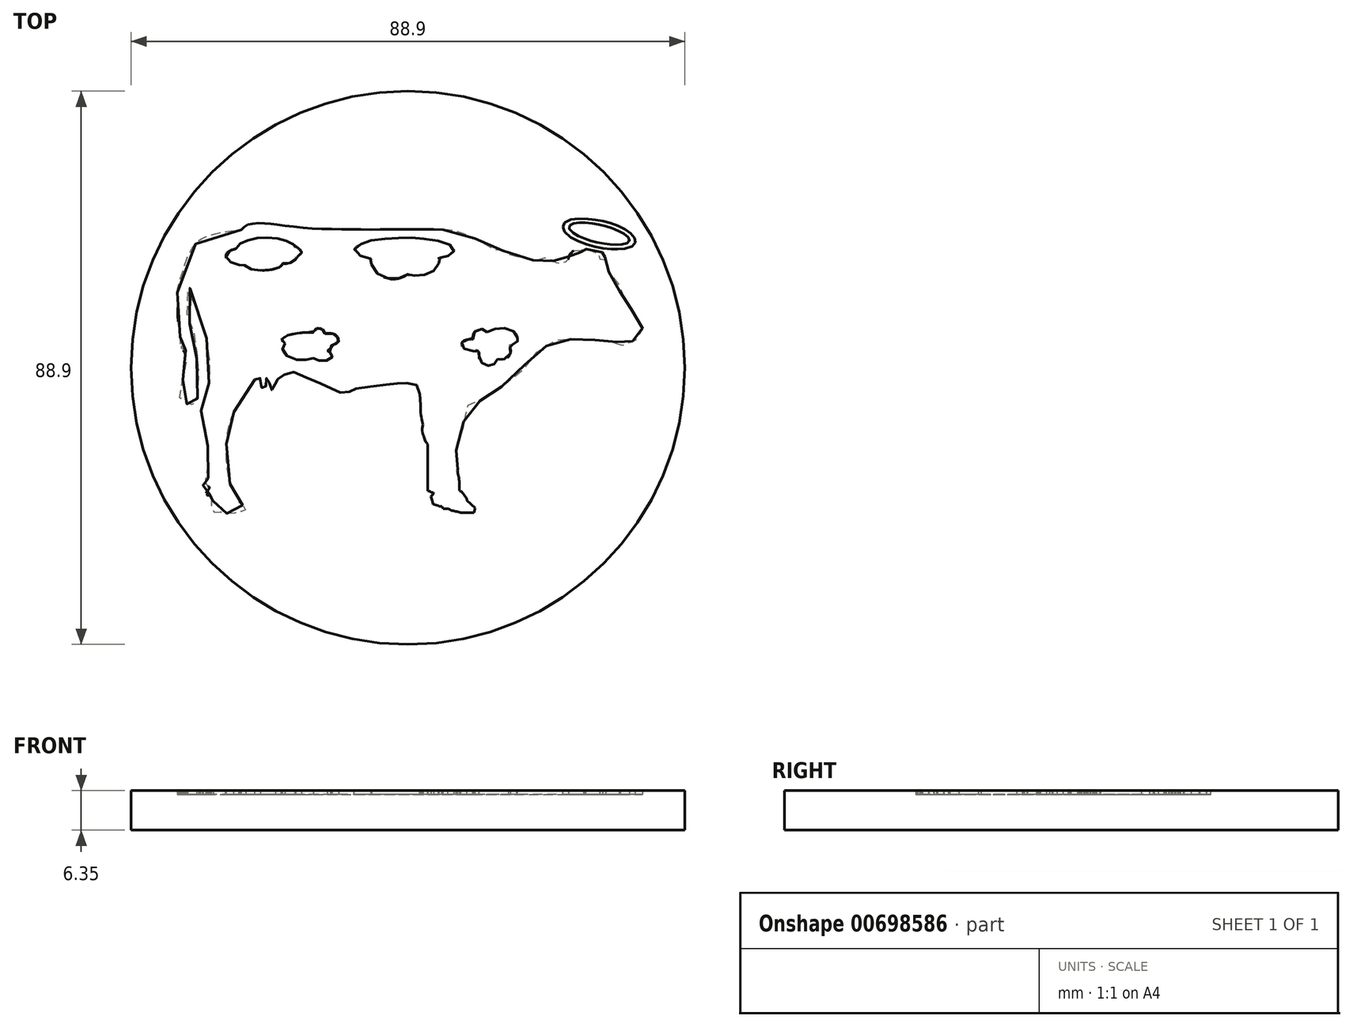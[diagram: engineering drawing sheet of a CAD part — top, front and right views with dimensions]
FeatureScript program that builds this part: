
annotation { "Feature Type Name" : "Feature", "Feature Type Description" : "" }
export const myFeature = defineFeature(function(context is Context, id is Id, definition is map)
    precondition{}
    {
        {
            var Q0;
            Q0=qCreatedBy(makeId("Top.planeOp"),FACE);
            var sketch = newSketch(context, id + "F0", { "sketchPlane" : qUnion([Q0])});
            skCircle(sketch, "E0", {"center": v(0, 0) * mm, "radius": 44.45 * mm});
            skSolve(sketch);
        }
        {
            var Q0;
            Q0=makeQuery(id+"F0.imprint","IMPRINT",FACE,{"disambiguationData":[TD([[makeQuery(id+"F0.imprint","IMPRINT",EDGE,{"derivedFrom":sQuery(id+"F0.wireOp",EDGE,"E0")}),1.0]])]});
            extrude(context, id + "F1", {"entities" : qUnion([Q0]), "depth" : 6.35 * mm, "offsetDistance" : 25.4 * mm});
        }
        {
            var Q0;
            Q0=makeQuery(id+"F1.opExtrude","CAP_FACE",FACE,{"disambiguationData":[OSD([sQuery(id+"F0.wireOp",EDGE,"E0")])],"isStart":false});
            var sketch = newSketch(context, id + "F2", { "sketchPlane" : qUnion([Q0])});
            skFitSpline(sketch, "E1", {"points": [v(-26.75, 22.15) * mm, v(-26.37, 22.53) * mm, v(-25.86, 22.91) * mm, v(-25.23, 23.1) * mm, v(-24.18, 23.23) * mm, v(-22.81, 23.17) * mm, v(-21.67, 23.07) * mm, v(-19.9, 22.85) * mm, v(-17.06, 22.53) * mm, v(-14.24, 22.34) * mm, v(-10.9, 22.28) * mm, v(-7.82, 22.22) * mm, v(-4.65, 22.22) * mm, v(-0.3, 22.25) * mm, v(5.62, 22.16) * mm], "startDerivative": vector(10.6, 11) * mm, "endDerivative": vector(16.74, -2.24) * mm});
            skFitSpline(sketch, "E2", {"points": [v(5.62, 22.16) * mm, v(7.08, 22.16) * mm, v(8.96, 21.52) * mm, v(10.79, 20.75) * mm, v(12.81, 19.7) * mm, v(13.87, 19.07) * mm, v(15.07, 18.87) * mm, v(15.6, 18.58) * mm, v(16.71, 18.1) * mm, v(18.5, 17.72) * mm, v(20.8, 17.19) * mm, v(21.24, 17.43) * mm, v(21.82, 17.67) * mm, v(22.63, 17.57) * mm, v(23.16, 17.28) * mm, v(23.64, 16.95) * mm, v(24.51, 16.85) * mm, v(25.28, 17.04) * mm, v(25.72, 17.33) * mm, v(25.76, 17.72) * mm, v(26.05, 18.3) * mm, v(26.53, 18.78) * mm, v(26.82, 18.97) * mm, v(27.4, 18.54) * mm, v(27.64, 18.15) * mm, v(27.74, 18.92) * mm, v(27.98, 18.68) * mm, v(28.27, 18.87) * mm, v(28.22, 19.02) * mm, v(28.32, 19.3) * mm, v(28.5, 19.55) * mm, v(28.5, 19.11) * mm, v(28.9, 19.11) * mm, v(29.57, 18.92) * mm, v(30.34, 18.54) * mm, v(30.58, 18.34) * mm, v(30.87, 18.54) * mm, v(31.1, 18.63) * mm, v(31.2, 18.34) * mm, v(30.92, 17.81) * mm, v(30.82, 17.48) * mm, v(30.92, 17.28) * mm, v(31.06, 17.57) * mm, v(31.3, 17.72) * mm, v(31.59, 17.81) * mm, v(31.73, 17.62) * mm, v(31.69, 17.33) * mm, v(31.25, 17.04) * mm, v(31.54, 16.75) * mm, v(31.83, 16.13) * mm, v(32.36, 15.31) * mm, v(32.8, 14.97) * mm, v(33.8, 13.82) * mm, v(33.9, 13.43) * mm, v(33.9, 12.7) * mm, v(34.1, 11.84) * mm, v(34.1, 11.55) * mm, v(34.72, 10.98) * mm, v(35.15, 10.4) * mm, v(35.78, 9.58) * mm, v(36.36, 8.76) * mm, v(37.22, 7.85) * mm, v(37.66, 7.17) * mm, v(37.66, 6.88) * mm, v(37.6, 5.78) * mm, v(37.18, 5.3) * mm, v(37.03, 5.3) * mm, v(36.84, 4.67) * mm, v(36.45, 4.43) * mm, v(36.07, 4.33) * mm, v(36.02, 4.1) * mm, v(35.4, 3.66) * mm, v(34.48, 3.56) * mm, v(34.1, 3.66) * mm, v(33.7, 3.85) * mm, v(33.42, 4.24) * mm, v(32.99, 4.14) * mm, v(32.12, 4.24) * mm, v(30.96, 4.38) * mm, v(30.34, 4.43) * mm, v(29.13, 4.62) * mm, v(28.22, 5) * mm, v(27.64, 4.76) * mm, v(26.49, 4.62) * mm, v(25.38, 4.62) * mm, v(24.7, 4.72) * mm, v(23.6, 4.28) * mm, v(22.3, 3.56) * mm, v(21.14, 2.84) * mm, v(19.8, 1.78) * mm, v(19.07, 1.1) * mm, v(18.35, -0.48) * mm, v(17.34, -1.6) * mm, v(15.94, -2.5) * mm, v(14.4, -3.42) * mm, v(13.87, -3.8) * mm, v(12.76, -4.62) * mm, v(12, -5.15) * mm, v(10.6, -5.64) * mm, v(9.58, -6.07) * mm, v(9.15, -7.51) * mm, v(8.86, -9.1) * mm, v(8.62, -10.74) * mm, v(8.28, -11.9) * mm, v(7.75, -13.24) * mm], "startDerivative": vector(72.15, 3.33) * mm, "endDerivative": vector(-42.6, -105.18) * mm});
            skLineSegment(sketch, "E3", {"start": v(7.75, -13.24) * mm, "end": v(7.97, -16.36) * mm});
            skFitSpline(sketch, "E4", {"points": [v(7.97, -16.36) * mm, v(7.97, -16.72) * mm, v(8.11, -17.41) * mm, v(8.24, -18.18) * mm, v(8.28, -18.83) * mm, v(8.32, -19.72) * mm, v(8.52, -19.88) * mm, v(8.96, -20.35) * mm, v(9.37, -20.98) * mm, v(9.47, -21.3) * mm], "startDerivative": vector(-0.27, -3.83) * mm, "endDerivative": vector(0.8, -3.53) * mm});
            skLineSegment(sketch, "E5", {"start": v(9.47, -21.3) * mm, "end": v(10.79, -22.54) * mm});
            skLineSegment(sketch, "E6", {"start": v(10.79, -22.54) * mm, "end": v(10.6, -23.28) * mm});
            skFitSpline(sketch, "E7", {"points": [v(10.6, -23.28) * mm, v(10, -23.28) * mm, v(9.13, -23.28) * mm, v(8.64, -23.28) * mm, v(7.87, -23.12) * mm, v(7.02, -22.92) * mm, v(6.43, -22.66) * mm], "startDerivative": vector(-3.63, -0.02) * mm, "endDerivative": vector(-3.47, 1.8) * mm});
            skLineSegment(sketch, "E8", {"start": v(6.43, -22.66) * mm, "end": v(5.62, -22.66) * mm});
            skLineSegment(sketch, "E9", {"start": v(5.62, -22.66) * mm, "end": v(5.44, -22.27) * mm});
            skFitSpline(sketch, "E10", {"points": [v(5.44, -22.27) * mm, v(5.06, -22.27) * mm, v(4.61, -22.07) * mm, v(4.27, -21.97) * mm, v(4.09, -21.93) * mm, v(3.92, -21.48) * mm, v(3.82, -21.08) * mm, v(3.7, -20.71) * mm, v(3.86, -20.47) * mm, v(4.1, -20.15) * mm, v(4.03, -20.07) * mm, v(3.78, -20.07) * mm, v(3.64, -19.92) * mm, v(3.44, -19.82) * mm, v(3.17, -19.8) * mm], "startDerivative": vector(-4.76, -0.6) * mm, "endDerivative": vector(-4.06, 0.05) * mm});
            skLineSegment(sketch, "E11", {"start": v(3.17, -19.8) * mm, "end": v(3.17, -12.8) * mm});
            skFitSpline(sketch, "E12", {"points": [v(3.17, -12.8) * mm, v(3.17, -12.33) * mm, v(2.91, -11.97) * mm, v(2.59, -11.16) * mm, v(2.39, -10.63) * mm, v(2.28, -9.8) * mm, v(2.4, -9.05) * mm, v(2.26, -8.55) * mm, v(2.1, -7.58) * mm, v(2.02, -6.79) * mm, v(2.02, -5.92) * mm], "startDerivative": vector(0.9, 6.21) * mm, "endDerivative": vector(0.15, 7.98) * mm});
            skFitSpline(sketch, "E13", {"points": [v(2.02, -5.92) * mm, v(2.02, -5.28) * mm, v(2.02, -4.67) * mm, v(1.82, -3.82) * mm, v(1.8, -2.9) * mm, v(1.45, -2.8) * mm, v(0.93, -2.6) * mm, v(0.69, -2.44) * mm, v(-0.35, -2.44) * mm, v(-0.87, -2.42) * mm, v(-1.46, -2.46) * mm, v(-1.9, -2.5) * mm, v(-2.61, -2.54) * mm, v(-3.32, -2.67) * mm, v(-4.74, -2.85) * mm, v(-6.32, -3.1) * mm, v(-7.43, -3.21) * mm, v(-8.53, -3.4) * mm, v(-8.9, -3.4) * mm, v(-9.13, -3.58) * mm, v(-9.36, -3.82) * mm, v(-9.88, -3.84) * mm, v(-10.25, -3.8) * mm, v(-10.8, -3.96) * mm, v(-11.36, -4) * mm, v(-11.9, -3.62) * mm, v(-12.37, -3.3) * mm, v(-12.98, -2.99) * mm, v(-14.03, -2.5) * mm, v(-15.1, -2.06) * mm, v(-16.74, -1.38) * mm, v(-17.84, -0.78) * mm, v(-18.56, -0.7) * mm, v(-19.14, -0.85) * mm, v(-19.61, -1.02) * mm, v(-20.2, -1.2) * mm, v(-20.36, -1.42) * mm, v(-20.57, -1.65) * mm, v(-20.89, -1.83) * mm, v(-21.12, -2) * mm, v(-21.27, -2.05) * mm, v(-21.3, -2.33) * mm, v(-21.32, -2.69) * mm, v(-21.37, -3.12) * mm, v(-21.45, -3.37) * mm, v(-21.63, -3.53) * mm, v(-21.95, -3.53) * mm, v(-22.15, -3.27) * mm, v(-22.25, -2.8) * mm, v(-22.33, -2.17) * mm, v(-22.43, -1.53) * mm, v(-22.56, -1.52) * mm, v(-22.67, -1.52) * mm, v(-22.7, -1.64) * mm, v(-22.72, -1.94) * mm, v(-22.73, -2.46) * mm, v(-22.78, -2.82) * mm, v(-22.84, -3.15) * mm, v(-22.97, -3.44) * mm, v(-23.28, -3.47) * mm, v(-23.44, -3.28) * mm, v(-23.63, -2.76) * mm, v(-23.72, -2.17) * mm, v(-23.74, -1.7) * mm, v(-23.96, -1.55) * mm, v(-24.14, -1.45) * mm, v(-24.3, -1.45) * mm, v(-24.6, -1.87) * mm], "startDerivative": vector(-0.98, 38.8) * mm, "endDerivative": vector(-19.04, -36.66) * mm});
            skLineSegment(sketch, "E14", {"start": v(-24.6, -1.87) * mm, "end": v(-27.93, -7.08) * mm});
            skFitSpline(sketch, "E15", {"points": [v(-27.93, -7.08) * mm, v(-28.21, -7.77) * mm, v(-28.5, -8.4) * mm, v(-28.68, -9) * mm, v(-28.92, -9.97) * mm, v(-29.04, -10.97) * mm, v(-29.17, -12.14) * mm, v(-29.23, -13.31) * mm, v(-29.2, -14.8) * mm, v(-29.09, -16.15) * mm, v(-28.86, -17.38) * mm, v(-28.58, -18.58) * mm, v(-28.28, -19.49) * mm, v(-27.79, -20.06) * mm, v(-27.42, -20.52) * mm, v(-27.14, -20.93) * mm, v(-27.12, -21.43) * mm, v(-27.18, -21.58) * mm, v(-26.9, -21.72) * mm, v(-26.57, -22.02) * mm, v(-26.29, -22.33) * mm, v(-26.07, -22.59) * mm, v(-26.19, -22.93) * mm, v(-26.39, -23.07) * mm, v(-26.71, -23.07) * mm, v(-27.12, -23.18) * mm, v(-27.93, -23.34) * mm, v(-28.74, -23.38) * mm, v(-29.75, -23.34) * mm, v(-30.22, -23.2) * mm, v(-30.74, -23.22) * mm, v(-31.05, -23.28) * mm, v(-31.3, -22.77) * mm, v(-31.55, -22.22) * mm, v(-31.55, -21.7) * mm, v(-31.41, -21.41) * mm, v(-31.27, -21.33) * mm, v(-31.29, -21.25) * mm, v(-31.43, -21.25) * mm, v(-31.7, -21.15) * mm, v(-31.63, -20.97) * mm, v(-31.6, -20.85) * mm, v(-31.61, -20.67) * mm, v(-31.73, -20.54) * mm, v(-31.82, -20.42) * mm, v(-32.02, -20.48) * mm, v(-32.24, -20.48) * mm, v(-32.3, -20.46) * mm, v(-32.18, -20.34) * mm, v(-32.02, -20.26) * mm, v(-31.88, -20.1) * mm, v(-32, -20.06) * mm, v(-32.18, -20.06) * mm, v(-32.34, -20.06) * mm, v(-32.44, -20.08) * mm, v(-32.36, -19.96) * mm, v(-32.16, -19.77) * mm, v(-32, -19.53) * mm, v(-31.88, -19.19) * mm, v(-32.12, -19.07) * mm, v(-32.48, -18.96) * mm, v(-32.83, -18.88) * mm, v(-33, -18.88) * mm, v(-32.75, -18.7) * mm, v(-32.56, -18.62) * mm, v(-32.38, -18.5) * mm, v(-32.28, -18.42) * mm, v(-32.73, -18.36) * mm, v(-32.87, -18.32) * mm, v(-32.9, -18.18) * mm, v(-32.69, -18.16) * mm, v(-32.5, -18.01) * mm, v(-32.38, -17.9) * mm, v(-32.16, -17.87) * mm, v(-32.1, -17.3) * mm, v(-32.1, -16.54) * mm, v(-32.08, -15.8) * mm, v(-32.08, -14.9) * mm, v(-32.12, -14) * mm, v(-32.12, -13.17) * mm, v(-32.18, -12.24) * mm, v(-32.26, -11.53) * mm, v(-32.36, -10.54) * mm, v(-32.5, -9.4) * mm, v(-32.85, -8.1) * mm, v(-33.2, -7.08) * mm, v(-33.35, -6.17) * mm, v(-33.32, -5.76) * mm, v(-33.04, -5.21) * mm, v(-32.51, -4.75) * mm, v(-32.45, -4.49) * mm, v(-32.23, -3.6) * mm, v(-31.94, -2.54) * mm, v(-31.7, -1.49) * mm, v(-31.66, -0.48) * mm, v(-31.74, 0.47) * mm, v(-32.06, 3) * mm, v(-32.47, 5.21) * mm, v(-32.9, 7.02) * mm, v(-33.1, 7.53) * mm, v(-34.17, 10.74) * mm, v(-35.08, 12.83) * mm, v(-35.28, 12.48) * mm, v(-35.43, 11.57) * mm, v(-35.54, 10.42) * mm, v(-35.54, 8.8) * mm, v(-35.31, 7.7) * mm, v(-34.74, 6.44) * mm, v(-34.37, 5.67) * mm, v(-34.1, 4.7) * mm, v(-33.97, 3.58) * mm, v(-33.94, 2.46) * mm, v(-33.9, 1.35) * mm, v(-33.76, 0.4) * mm, v(-33.65, -0.63) * mm, v(-33.6, -2.29) * mm, v(-33.68, -3.66) * mm, v(-33.82, -4.98) * mm, v(-33.97, -5.3) * mm, v(-34.17, -5.53) * mm, v(-34.42, -5.55) * mm, v(-34.6, -5.87) * mm, v(-34.77, -6.16) * mm, v(-35.11, -6.3) * mm, v(-35.25, -6.07) * mm, v(-35.37, -5.67) * mm, v(-35.37, -5.47) * mm, v(-35.6, -5.9) * mm, v(-35.97, -5.98) * mm, v(-36.34, -5.78) * mm, v(-36.54, -5.44) * mm, v(-36.66, -4.75) * mm, v(-36.66, -3.95) * mm, v(-36.37, -2.86) * mm, v(-36.08, -1.63) * mm, v(-35.91, -0.57) * mm, v(-35.68, 0.69) * mm, v(-35.51, 1.35) * mm, v(-35.68, 1.35) * mm, v(-35.74, 1.6) * mm, v(-35.74, 1.98) * mm, v(-35.71, 2.84) * mm, v(-36.03, 2.63) * mm, v(-36.06, 2.92) * mm, v(-36.03, 3.24) * mm, v(-36.28, 3.04) * mm, v(-36.28, 3.52) * mm, v(-36.26, 3.9) * mm, v(-36.46, 3.64) * mm, v(-36.51, 4.3) * mm, v(-36.63, 5.53) * mm, v(-36.77, 6.61) * mm, v(-36.94, 8.19) * mm, v(-36.97, 10.22) * mm, v(-37.03, 12) * mm, v(-36.74, 13.57) * mm, v(-36.14, 15.52) * mm, v(-35.29, 18) * mm, v(-34.03, 19.98) * mm, v(-32.97, 20.84) * mm, v(-30.97, 21.52) * mm, v(-28.89, 21.9) * mm, v(-26.75, 22.15) * mm], "startDerivative": vector(-40.9, -104.55) * mm, "endDerivative": vector(191.28, 19.96) * mm});
            skFitSpline(sketch, "E16", {"points": [v(-27.53, 19.17) * mm, v(-27.4, 19.48) * mm, v(-26.95, 19.94) * mm, v(-26.25, 20.3) * mm, v(-25.46, 20.56) * mm, v(-24.18, 20.85) * mm, v(-23.08, 20.9) * mm, v(-21.73, 20.85) * mm, v(-20.4, 20.66) * mm, v(-19.54, 20.42) * mm, v(-18.7, 20.06) * mm, v(-18.28, 19.67) * mm, v(-18.1, 19.38) * mm, v(-17.47, 19.19) * mm, v(-17.2, 18.95) * mm, v(-17.03, 18.56) * mm, v(-17.08, 18.27) * mm, v(-17.51, 17.96) * mm, v(-18.1, 17.77) * mm, v(-17.97, 17.6) * mm, v(-18.1, 17.31) * mm, v(-18.48, 17.05) * mm, v(-19.22, 16.78) * mm, v(-19.9, 16.73) * mm, v(-20.1, 16.78) * mm, v(-20.28, 16.5) * mm, v(-20.7, 16.16) * mm, v(-21.41, 15.87) * mm, v(-22.62, 15.7) * mm, v(-23.92, 15.65) * mm, v(-25.07, 15.84) * mm, v(-25.97, 16.2) * mm, v(-26.25, 16.52) * mm, v(-26.45, 16.5) * mm, v(-27, 16.52) * mm, v(-27.93, 16.76) * mm, v(-28.66, 17.17) * mm, v(-29.17, 17.7) * mm, v(-29.22, 18.18) * mm, v(-28.83, 18.64) * mm, v(-28.18, 18.97) * mm, v(-27.53, 19.17) * mm]});
            skFitSpline(sketch, "E17", {"points": [v(-19.28, 5.22) * mm, v(-18.55, 5.42) * mm, v(-17.65, 5.58) * mm, v(-16.88, 5.65) * mm, v(-15.96, 5.68) * mm, v(-15.1, 5.68) * mm, v(-15.1, 5.83) * mm, v(-15.06, 5.99) * mm, v(-14.94, 6.12) * mm, v(-14.74, 6.26) * mm, v(-14.5, 6.33) * mm, v(-14.22, 6.36) * mm, v(-13.97, 6.3) * mm, v(-13.78, 6.2) * mm, v(-13.61, 5.99) * mm, v(-13.5, 5.75) * mm, v(-13.42, 5.53) * mm, v(-13.1, 5.5) * mm, v(-12.49, 5.54) * mm, v(-11.9, 5.46) * mm, v(-11.52, 5.24) * mm, v(-11.31, 4.96) * mm, v(-11.28, 4.78) * mm, v(-11.14, 4.62) * mm, v(-11.07, 4.45) * mm, v(-11.13, 4.22) * mm, v(-11.38, 3.96) * mm, v(-11.65, 3.82) * mm, v(-11.96, 3.69) * mm, v(-12.35, 3.6) * mm, v(-12.32, 3.48) * mm, v(-12.33, 3.3) * mm, v(-12.5, 3.06) * mm, v(-12.91, 2.67) * mm, v(-12.7, 2.6) * mm, v(-12.35, 2.4) * mm, v(-12.18, 2.14) * mm, v(-12.13, 1.85) * mm, v(-12.23, 1.6) * mm, v(-12.68, 1.27) * mm, v(-13.13, 1.13) * mm, v(-13.8, 1.13) * mm, v(-14.17, 1.13) * mm, v(-14.67, 1.3) * mm, v(-14.94, 1.58) * mm, v(-15.2, 1.53) * mm, v(-15.72, 1.34) * mm, v(-16.18, 1.29) * mm, v(-16.88, 1.29) * mm, v(-17.65, 1.29) * mm, v(-18.6, 1.5) * mm, v(-19.55, 1.99) * mm, v(-20.05, 2.51) * mm, v(-20.15, 2.99) * mm, v(-19.98, 3.45) * mm, v(-19.69, 3.8) * mm, v(-19.84, 3.9) * mm, v(-20.18, 4.1) * mm, v(-20.32, 4.45) * mm, v(-20.2, 4.73) * mm, v(-19.86, 5.02) * mm, v(-19.28, 5.22) * mm]});
            skFitSpline(sketch, "E18", {"points": [v(12.7, 5.74) * mm, v(13.14, 6.04) * mm, v(13.89, 6.25) * mm, v(14.68, 6.35) * mm, v(15.55, 6.35) * mm, v(16.38, 6.13) * mm, v(17.04, 5.78) * mm, v(17.48, 5.32) * mm, v(17.6, 4.87) * mm, v(17.54, 4.6) * mm, v(17.5, 4.5) * mm, v(17.55, 4.48) * mm, v(17.6, 4.4) * mm, v(17.6, 4.24) * mm, v(17.38, 4) * mm, v(17.04, 3.8) * mm, v(16.64, 3.66) * mm, v(16.2, 3.6) * mm, v(16.24, 3.5) * mm, v(16.36, 3.28) * mm, v(16.48, 3) * mm, v(16.5, 2.65) * mm, v(16.4, 2.22) * mm, v(16.1, 1.75) * mm, v(15.55, 1.4) * mm, v(14.96, 1.22) * mm, v(14.42, 1.29) * mm, v(14.37, 1.33) * mm, v(14.3, 1.16) * mm, v(14.15, 0.91) * mm, v(13.84, 0.63) * mm, v(13.59, 0.49) * mm, v(13.32, 0.36) * mm, v(12.96, 0.33) * mm, v(12.54, 0.39) * mm, v(12.08, 0.6) * mm, v(11.68, 1) * mm, v(11.48, 1.42) * mm, v(11.41, 1.83) * mm, v(11.43, 2.17) * mm, v(11.43, 2.49) * mm, v(11.38, 2.55) * mm, v(11.24, 2.65) * mm, v(11.14, 2.8) * mm, v(10.9, 2.72) * mm, v(10.5, 2.68) * mm, v(9.8, 2.75) * mm, v(9.03, 3.05) * mm, v(8.6, 3.48) * mm, v(8.58, 3.9) * mm, v(8.88, 4.26) * mm, v(9.38, 4.48) * mm, v(9.88, 4.6) * mm, v(10.25, 4.62) * mm, v(10.5, 4.62) * mm, v(10.45, 4.82) * mm, v(10.45, 5.14) * mm, v(10.55, 5.52) * mm, v(10.82, 5.87) * mm, v(11.24, 6.15) * mm, v(11.85, 6.23) * mm, v(12.16, 6.14) * mm, v(12.54, 5.9) * mm, v(12.7, 5.74) * mm]});
            skFitSpline(sketch, "E19", {"points": [v(-5.88, 20.44) * mm, v(-4.67, 20.63) * mm, v(-2.95, 20.75) * mm, v(-1.68, 20.85) * mm, v(-0.26, 20.9) * mm, v(0.84, 20.92) * mm, v(2.02, 20.8) * mm, v(3.55, 20.63) * mm, v(5.1, 20.34) * mm, v(6.27, 19.96) * mm, v(7.1, 19.52) * mm, v(7.45, 19.13) * mm, v(7.38, 18.74) * mm, v(7.18, 18.41) * mm, v(6.85, 18.18) * mm, v(6.43, 17.97) * mm, v(5.83, 17.8) * mm, v(5.32, 17.65) * mm, v(4.93, 17.63) * mm, v(4.95, 17.46) * mm, v(4.98, 17.03) * mm, v(4.84, 16.5) * mm, v(4.5, 16) * mm, v(4.01, 15.54) * mm, v(3.45, 15.25) * mm, v(2.67, 14.96) * mm, v(1.87, 14.84) * mm, v(1.08, 14.79) * mm, v(0.45, 14.84) * mm, v(0.15, 14.94) * mm, v(0, 15) * mm, v(-0.35, 14.8) * mm, v(-0.88, 14.55) * mm, v(-1.6, 14.33) * mm, v(-2.65, 14.26) * mm, v(-3.87, 14.57) * mm, v(-4.77, 15.03) * mm, v(-5.42, 15.7) * mm, v(-5.8, 16.52) * mm, v(-5.88, 17.02) * mm, v(-5.81, 17.51) * mm, v(-5.91, 17.55) * mm, v(-6.5, 17.66) * mm, v(-7.23, 17.85) * mm, v(-8.23, 18.38) * mm, v(-8.59, 18.82) * mm, v(-8.57, 19.16) * mm, v(-8.28, 19.57) * mm, v(-7.55, 19.91) * mm, v(-6.72, 20.17) * mm, v(-5.88, 20.44) * mm]});
            skFitSpline(sketch, "E20", {"points": [v(24.88, 22.6) * mm, v(24.9, 22.83) * mm, v(25.05, 23.22) * mm, v(25.63, 23.63) * mm, v(26.36, 23.85) * mm, v(27.38, 23.97) * mm, v(28.76, 23.92) * mm, v(29.53, 23.87) * mm, v(30.35, 23.75) * mm, v(31.2, 23.6) * mm, v(32.13, 23.37) * mm, v(33.02, 23.08) * mm, v(34.02, 22.68) * mm, v(34.82, 22.28) * mm, v(35.4, 21.88) * mm, v(35.96, 21.4) * mm, v(36.27, 21) * mm, v(36.44, 20.7) * mm, v(36.53, 20.41) * mm, v(36.5, 20.09) * mm, v(36.29, 19.75) * mm, v(35.93, 19.46) * mm, v(34.92, 19.13) * mm, v(34.24, 19.08) * mm, v(33.43, 19.07) * mm, v(32.8, 19.07) * mm, v(31.95, 19.1) * mm, v(30.82, 19.27) * mm, v(29.97, 19.46) * mm, v(28.81, 19.78) * mm, v(27.74, 20.16) * mm, v(26.53, 20.73) * mm, v(25.7, 21.28) * mm, v(25.08, 21.94) * mm, v(24.9, 22.37) * mm, v(24.88, 22.6) * mm]});
            skFitSpline(sketch, "E21", {"points": [v(25.97, 22.9) * mm, v(26.26, 23.08) * mm, v(26.7, 23.2) * mm, v(27.31, 23.29) * mm, v(28.01, 23.32) * mm, v(28.86, 23.32) * mm, v(30, 23.13) * mm, v(30.9, 22.98) * mm, v(31.9, 22.73) * mm, v(32.75, 22.44) * mm, v(33.55, 22.08) * mm, v(34.31, 21.74) * mm, v(34.9, 21.38) * mm, v(35.4, 20.94) * mm, v(35.59, 20.6) * mm, v(35.59, 20.46) * mm, v(35.47, 20.2) * mm, v(35.21, 20.04) * mm, v(34.65, 19.87) * mm, v(34.12, 19.8) * mm, v(33.4, 19.76) * mm, v(32.7, 19.8) * mm, v(32, 19.87) * mm, v(31.16, 19.99) * mm, v(30.07, 20.22) * mm, v(29.22, 20.45) * mm, v(28.35, 20.77) * mm, v(27.57, 21.07) * mm, v(26.82, 21.47) * mm, v(26.3, 21.9) * mm, v(25.88, 22.33) * mm, v(25.82, 22.56) * mm, v(25.97, 22.9) * mm]});
            skSolve(sketch);
        }
        {
            var Q0;
            Q0 = qSketchRegion(id + "F2", true);
            extrude(context, id + "F3", {"entities" : qUnion([Q0]), "operationType" : NewBodyOperationType.REMOVE, "oppositeDirection" : true, "depth" : 0.64 * mm, "offsetDistance" : 25.4 * mm});
        }
    });
